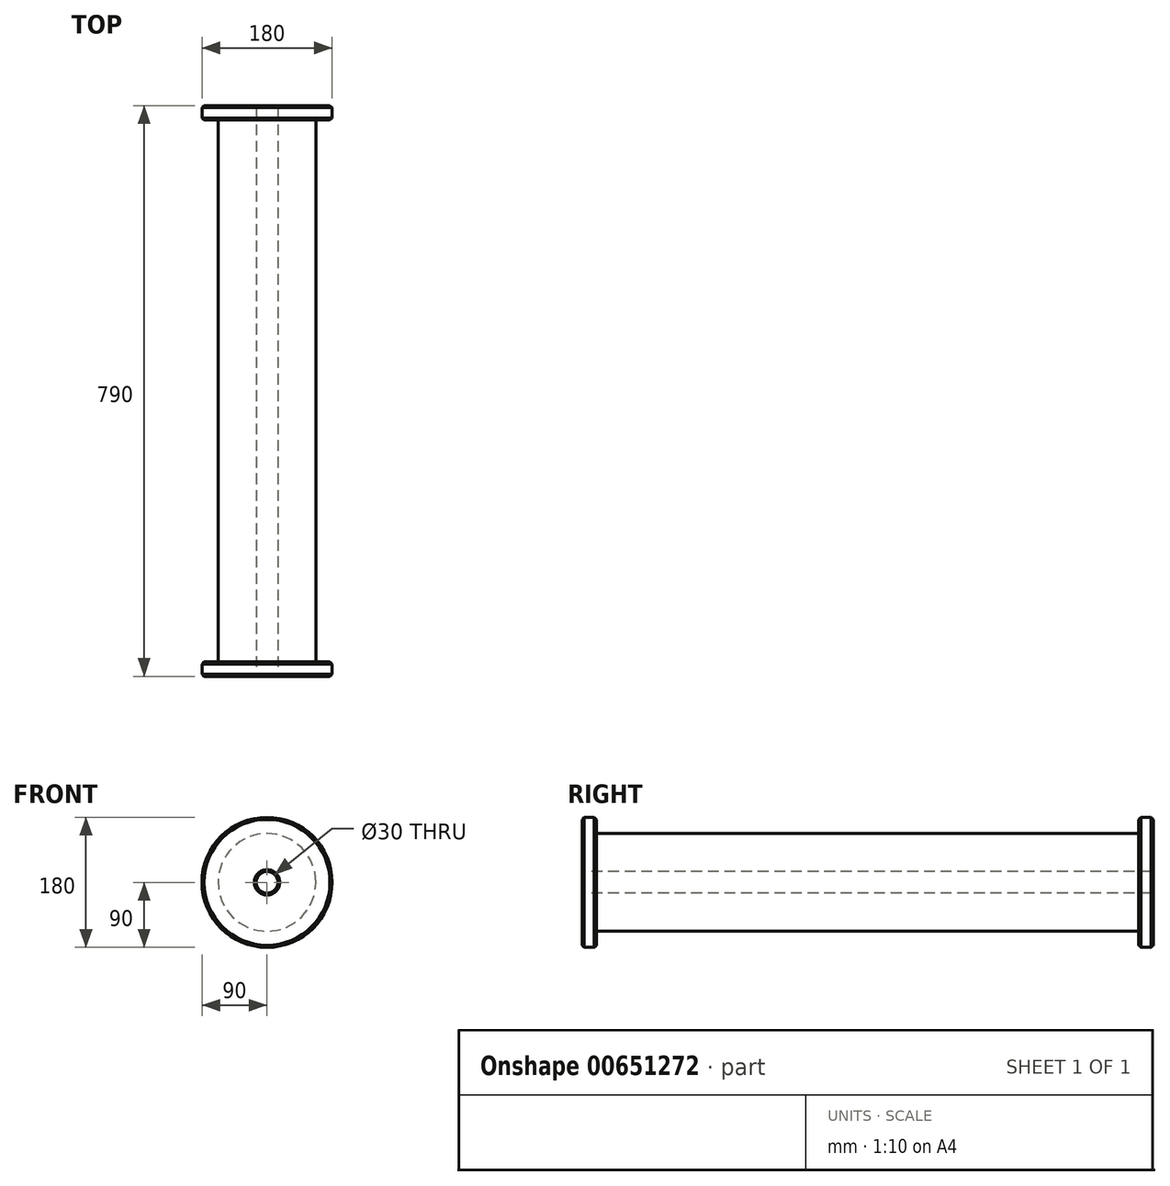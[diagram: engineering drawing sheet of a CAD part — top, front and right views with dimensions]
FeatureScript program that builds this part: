
annotation { "Feature Type Name" : "Feature", "Feature Type Description" : "" }
export const myFeature = defineFeature(function(context is Context, id is Id, definition is map)
    precondition{}
    {
        {
            var Q0;
            Q0=qCreatedBy(makeId("Front.planeOp"),FACE);
            var sketch = newSketch(context, id + "F0", { "sketchPlane" : qUnion([Q0])});
            skCircle(sketch, "E0", {"center": v(0, 0) * mm, "radius": 90 * mm});
            skSolve(sketch);
        }
        {
            var Q0;
            Q0 = qSketchRegion(id + "F0", true);
            extrude(context, id + "F1", {"entities" : qUnion([Q0]), "depth" : 20 * mm, "offsetDistance" : 25.4 * mm});
        }
        {
            var Q0;
            Q0=makeQuery(id+"F1.opExtrude","CAP_FACE",FACE,{"disambiguationData":[OSD([sQuery(id+"F0.wireOp",EDGE,"E0")])],"isStart":false});
            var sketch = newSketch(context, id + "F2", { "sketchPlane" : qUnion([Q0])});
            skCircle(sketch, "E1", {"center": v(0, 0) * mm, "radius": 67.5 * mm});
            skSolve(sketch);
        }
        {
            var Q0;
            Q0 = qSketchRegion(id + "F2", true);
            extrude(context, id + "F3", {"entities" : qUnion([Q0]), "operationType" : NewBodyOperationType.ADD, "depth" : 750 * mm, "offsetDistance" : 25.4 * mm});
        }
        {
            var Q0;
            Q0=makeQuery(id+"F3.opExtrude","CAP_FACE",FACE,{"disambiguationData":[OSD([sQuery(id+"F2.wireOp",EDGE,"E1")])],"isStart":false});
            var sketch = newSketch(context, id + "F4", { "sketchPlane" : qUnion([Q0])});
            skCircle(sketch, "E2", {"center": v(0, 0) * mm, "radius": 90 * mm});
            skSolve(sketch);
        }
        {
            var Q0;
            Q0 = qSketchRegion(id + "F4", true);
            extrude(context, id + "F5", {"entities" : qUnion([Q0]), "operationType" : NewBodyOperationType.ADD, "depth" : 20 * mm, "offsetDistance" : 25.4 * mm});
        }
        {
            var Q0;
            Q0=makeQuery(id+"F5.opExtrude","CAP_FACE",FACE,{"disambiguationData":[OSD([sQuery(id+"F4.wireOp",EDGE,"E2")])],"isStart":false});
            var sketch = newSketch(context, id + "F6", { "sketchPlane" : qUnion([Q0])});
            skPoint(sketch, "E3", {"position": v(0, 0) * mm});
            skSolve(sketch);
        }
        {
            var Q0;
            Q0=sQuery(id+"F6.wireOp",VERTEX,"E3");
            var Q1;
            Q1=makeQuery(id+"F1.opExtrude","SWEPT_BODY",BODY,{"disambiguationData":[OSD([sQuery(id+"F0.wireOp",EDGE,"E0")])]});
            hole(context, id + "F7", {"style" : HoleStyle.C_SINK, "endStyle" : HoleEndStyle.THROUGH, "holeDiameter" : 30 * mm, "cSinkDiameter" : 35 * mm, "cSinkAngle" : 90 * degree, "majorDiameter" : 5 * mm, "isTappedThrough" : true, "tappedDepth" : 12.7 * mm, "tapClearance" : 3, "locations" : qUnion([Q0]), "scope" : qUnion([Q1])});
        }
        {
            var Q0;
            Q0=makeQuery(id+"F1.opExtrude","CAP_FACE",FACE,{"disambiguationData":[OSD([sQuery(id+"F0.wireOp",EDGE,"E0")])],"isStart":true});
            var Q1;
            Q1=makeQuery(id+"F1.opExtrude","CAP_EDGE",EDGE,{"disambiguationData":[OSD([sQuery(id+"F0.wireOp",EDGE,"E0")])],"isStart":false});
            chamfer(context, id + "F8", {"entities" : qUnion([Q0, Q1]), "width" : 3 * mm, "tangentPropagation" : true});
        }
        {
            var Q0;
            Q0=makeQuery(id+"F5.opExtrude","CAP_EDGE",EDGE,{"disambiguationData":[OSD([sQuery(id+"F4.wireOp",EDGE,"E2")])],"isStart":true});
            var Q1;
            Q1=makeQuery(id+"F5.opExtrude","CAP_EDGE",EDGE,{"disambiguationData":[OSD([sQuery(id+"F4.wireOp",EDGE,"E2")])],"isStart":false});
            chamfer(context, id + "F9", {"entities" : qUnion([Q0, Q1]), "width" : 3 * mm, "tangentPropagation" : true});
        }
    });
